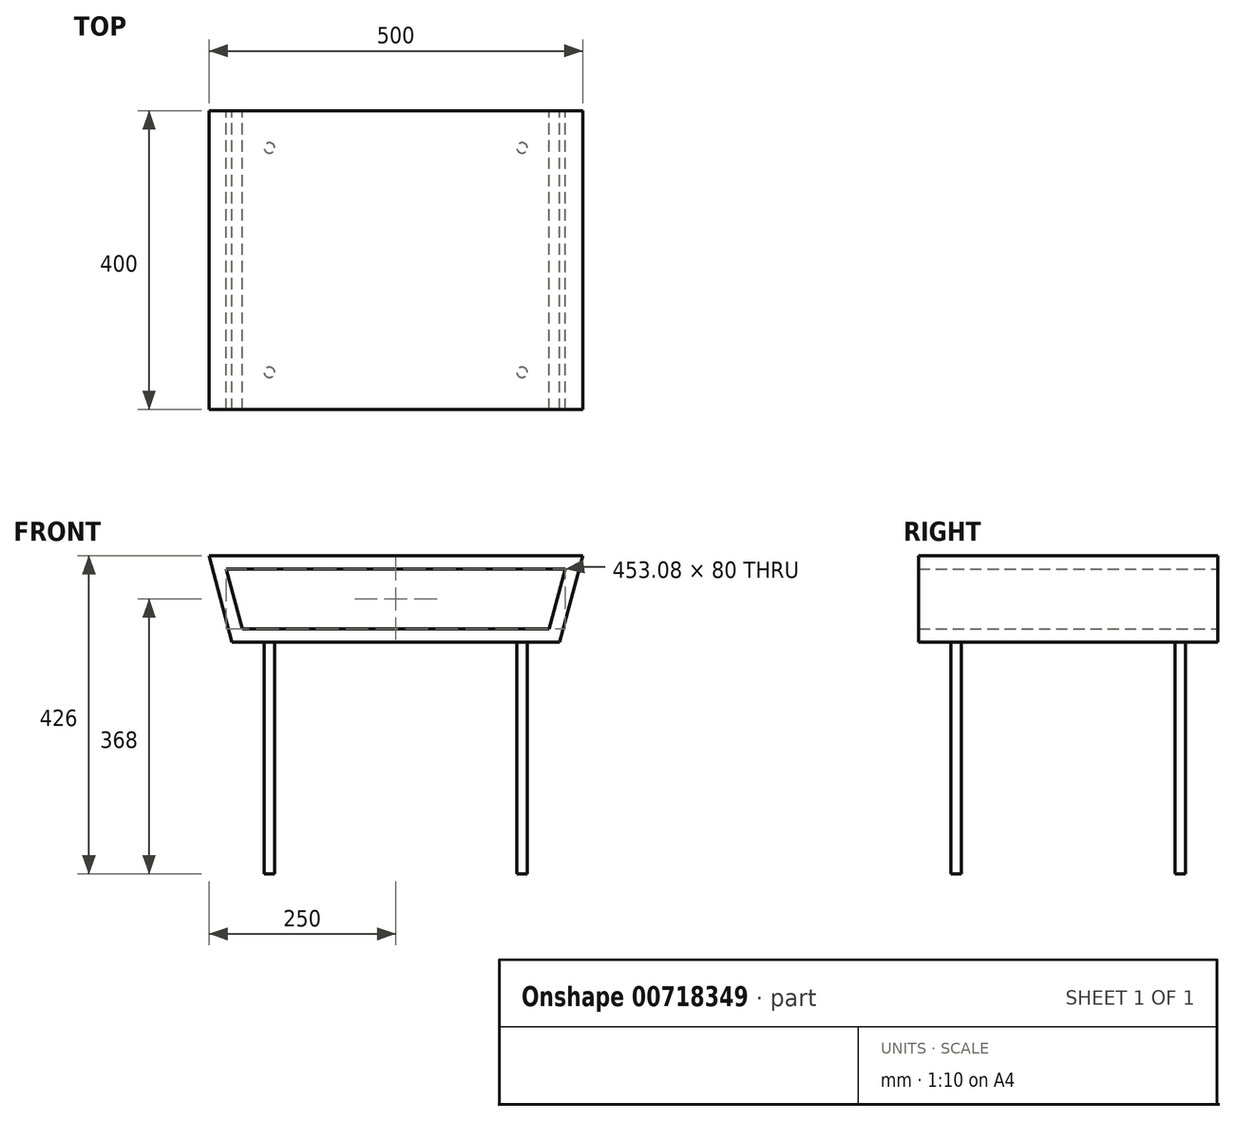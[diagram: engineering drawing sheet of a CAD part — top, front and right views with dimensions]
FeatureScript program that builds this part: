
annotation { "Feature Type Name" : "Feature", "Feature Type Description" : "" }
export const myFeature = defineFeature(function(context is Context, id is Id, definition is map)
    precondition{}
    {
        {
            var Q0;
            Q0=qCreatedBy(makeId("Front.planeOp"),FACE);
            var sketch = newSketch(context, id + "F0", { "sketchPlane" : qUnion([Q0])});
            skLineSegment(sketch, "E0.bottom", {"start": v(-218.92, 0) * mm, "end": v(218.92, 0) * mm});
            skLineSegment(sketch, "E0.top", {"start": v(-250, 116) * mm, "end": v(250, 116) * mm});
            skPoint(sketch, "E1", {"position": v(0, 0) * mm});
            skLineSegment(sketch, "E2.1", {"start": v(-223.74, 18) * mm, "end": v(223.74, 18) * mm});
            skLineSegment(sketch, "E2.3", {"start": v(-245.18, 98) * mm, "end": v(245.18, 98) * mm});
            skLineSegment(sketch, "E3", {"start": v(-223.74, 18) * mm, "end": v(-218.92, 0) * mm});
            skLineSegment(sketch, "E4", {"start": v(218.92, 0) * mm, "end": v(223.74, 18) * mm});
            skLineSegment(sketch, "E5", {"start": v(-245.18, 98) * mm, "end": v(-223.74, 18) * mm});
            skLineSegment(sketch, "E6", {"start": v(-226.54, 98) * mm, "end": v(-205.1, 18) * mm});
            skLineSegment(sketch, "E7", {"start": v(-250, 116) * mm, "end": v(-245.18, 98) * mm});
            skLineSegment(sketch, "E8", {"start": v(250, 116) * mm, "end": v(245.18, 98) * mm});
            skPoint(sketch, "E9", {"position": v(0, 116) * mm});
            skLineSegment(sketch, "E10", {"start": v(0, 0) * mm, "end": v(0, 211.43) * mm, "construction": true});
            skLineSegment(sketch, "E11", {"start": v(223.74, 18) * mm, "end": v(245.18, 98) * mm});
            skLineSegment(sketch, "E12", {"start": v(205.1, 18) * mm, "end": v(226.54, 98) * mm});
            skSolve(sketch);
        }
        {
            var Q0;
            Q0=makeQuery(id+"F0.imprint","IMPRINT",FACE,{"disambiguationData":[TD([[makeQuery(id+"F0.imprint","IMPRINT",EDGE,{"derivedFrom":sQuery(id+"F0.wireOp",EDGE,"E0.top")}),-1.0]])]});
            var Q1;
            {var subQ0=sQuery(id+"F0.wireOp",EDGE,"E5");Q1=makeQuery(id+"F0.imprint","IMPRINT",FACE,{"disambiguationData":[TD([[makeQuery(id+"F0.imprint","IMPRINT",EDGE,{"derivedFrom":subQ0}),1.0]])]});}
            var Q2;
            Q2=makeQuery(id+"F0.imprint","IMPRINT",FACE,{"disambiguationData":[TD([[makeQuery(id+"F0.imprint","IMPRINT",EDGE,{"derivedFrom":sQuery(id+"F0.wireOp",EDGE,"E0.bottom")}),1.0]])]});
            var Q3;
            {var subQ0=sQuery(id+"F0.wireOp",EDGE,"E11");Q3=makeQuery(id+"F0.imprint","IMPRINT",FACE,{"disambiguationData":[TD([[makeQuery(id+"F0.imprint","IMPRINT",EDGE,{"derivedFrom":subQ0}),1.0]])]});}
            extrude(context, id + "F1", {"entities" : qUnion([Q0, Q1, Q2, Q3]), "depth" : 400 * mm, "offsetDistance" : 25 * mm});
        }
        {
            var Q0;
            Q0=makeQuery(id+"F1.opExtrude","SWEPT_FACE",FACE,{"disambiguationData":[OSD([sQuery(id+"F0.wireOp",EDGE,"E0.bottom")])]});
            var sketch = newSketch(context, id + "F2", { "sketchPlane" : qUnion([Q0])});
            skLineSegment(sketch, "E13", {"start": v(-650.42, 200) * mm, "end": v(637.73, 200) * mm, "construction": true});
            skPoint(sketch, "E13.startSnap0", {"position": v(-218.92, 200) * mm});
            skLineSegment(sketch, "E14", {"start": v(0, -55.7) * mm, "end": v(0, 743.64) * mm, "construction": true});
            skPoint(sketch, "E14.endSnap0", {"position": v(0, 400) * mm});
            skCircle(sketch, "E15", {"center": v(-168.92, 50) * mm, "radius": 7 * mm});
            skCircle(sketch, "E16.MirrorC", {"center": v(-168.92, 350) * mm, "radius": 7 * mm});
            skCircle(sketch, "E17.MirrorC", {"center": v(168.92, 50) * mm, "radius": 7 * mm});
            skCircle(sketch, "E18.MirrorC", {"center": v(168.92, 350) * mm, "radius": 7 * mm});
            skSolve(sketch);
        }
        {
            var Q0;
            Q0=qSketchRegion(id+"F2",true);
            extrude(context, id + "F3", {"entities" : qUnion([Q0]), "depth" : 310 * mm, "offsetDistance" : 25 * mm});
        }
    });
